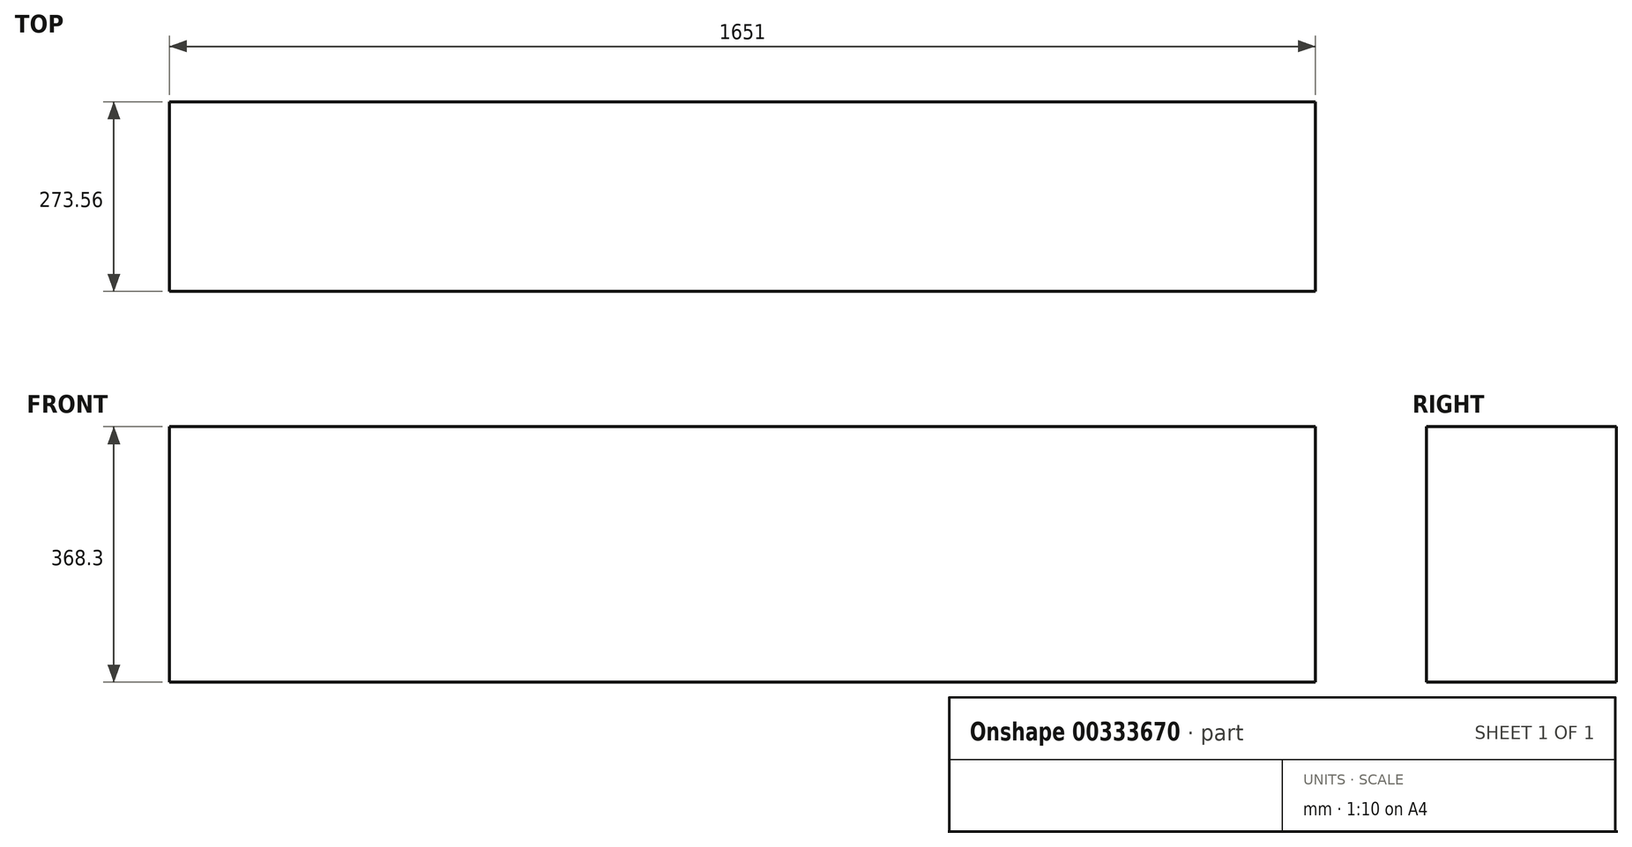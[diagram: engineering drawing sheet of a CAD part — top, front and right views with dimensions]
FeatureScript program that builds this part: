
annotation { "Feature Type Name" : "Feature", "Feature Type Description" : "" }
export const myFeature = defineFeature(function(context is Context, id is Id, definition is map)
    precondition{}
    {
        {
            var Q0;
            Q0=qCreatedBy(makeId("Front.planeOp"),FACE);
            var sketch = newSketch(context, id + "F0", { "sketchPlane" : qUnion([Q0])});
            skLineSegment(sketch, "E0.bottom", {"start": v(-825.5, 184.15) * mm, "end": v(825.5, 184.15) * mm});
            skLineSegment(sketch, "E0.top", {"start": v(-825.5, -184.15) * mm, "end": v(825.5, -184.15) * mm});
            skLineSegment(sketch, "E0.left", {"start": v(-825.5, 184.15) * mm, "end": v(-825.5, -184.15) * mm});
            skLineSegment(sketch, "E0.right", {"start": v(825.5, 184.15) * mm, "end": v(825.5, -184.15) * mm});
            skPoint(sketch, "E0.middle", {"position": v(0, 0) * mm});
            skSolve(sketch);
        }
        {
            var Q0;
            Q0=makeQuery(id+"F0.imprint","IMPRINT",FACE,{"disambiguationData":[TD([[makeQuery(id+"F0.imprint","IMPRINT",EDGE,{"derivedFrom":sQuery(id+"F0.wireOp",EDGE,"E0.bottom")}),-1.0]])]});
            extrude(context, id + "F1", {"entities" : qUnion([Q0]), "depth" : 273.56 * mm});
        }
    });
